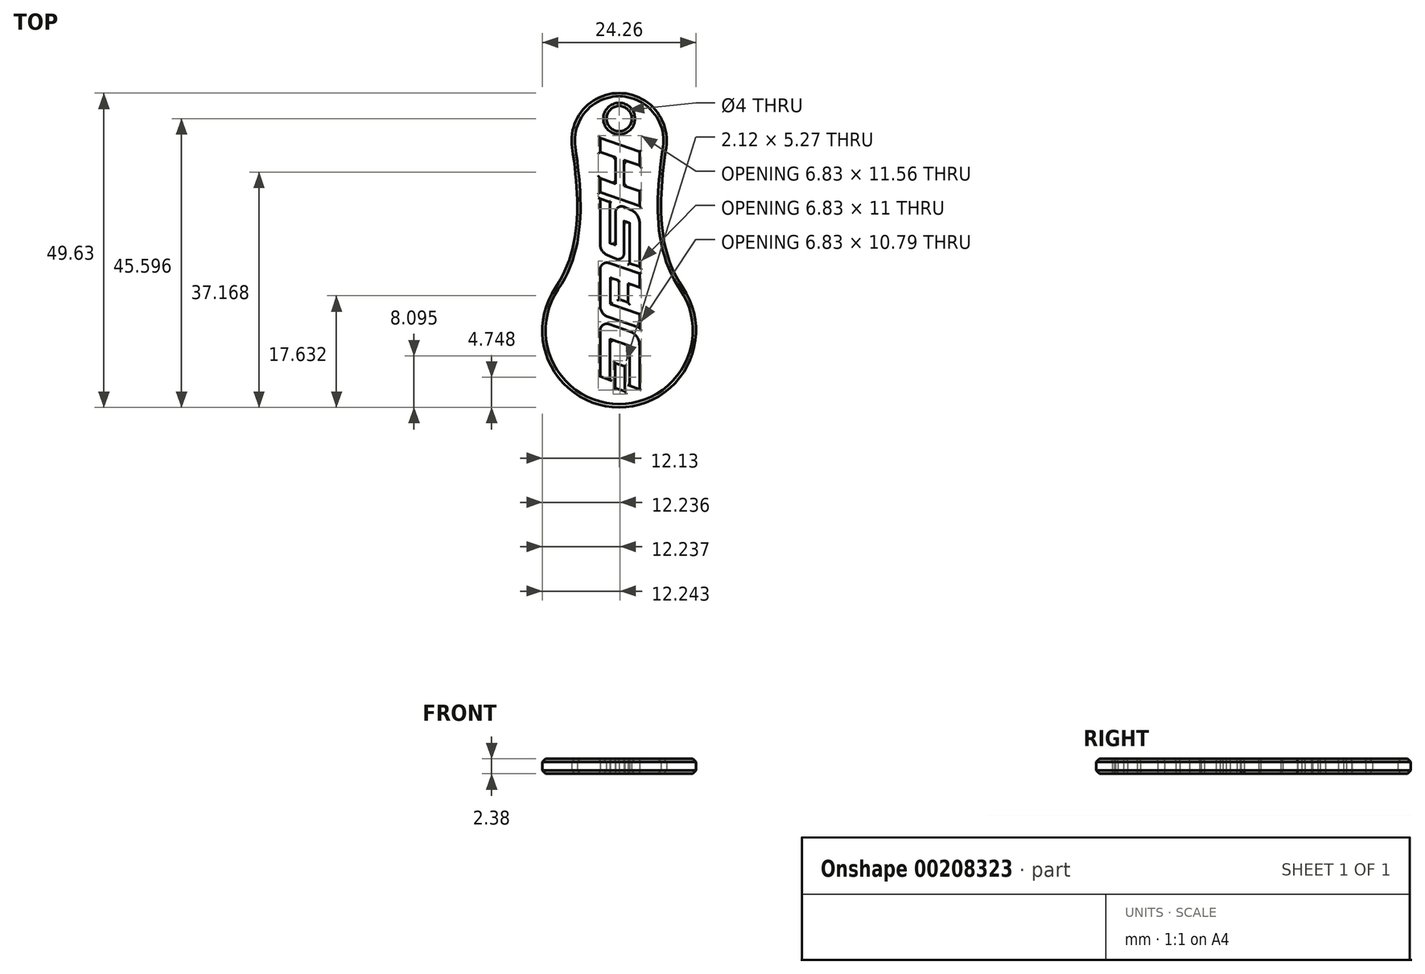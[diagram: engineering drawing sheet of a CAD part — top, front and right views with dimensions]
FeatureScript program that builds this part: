
annotation { "Feature Type Name" : "Feature", "Feature Type Description" : "" }
export const myFeature = defineFeature(function(context is Context, id is Id, definition is map)
    precondition{}
    {
        {
            var Q0;
            Q0=qCreatedBy(makeId("Top.planeOp"),FACE);
            var sketch = newSketch(context, id + "F0", { "sketchPlane" : qUnion([Q0])});
            skArc(sketch, "E0", {"start": v(-10.03, 6.81) * mm, "mid": v(0, -12.13) * mm, "end": v(10.03, 6.81) * mm});
            skLineSegment(sketch, "E1", {"start": v(0, 0) * mm, "end": v(0, 30) * mm, "construction": true});
            skArc(sketch, "E2", {"start": v(7.42, 28.91) * mm, "mid": v(0, 37.5) * mm, "end": v(-7.42, 28.91) * mm});
            skFitSpline(sketch, "E3", {"points": [v(-7.42, 28.91) * mm, v(-10.03, 6.81) * mm], "startDerivative": vector(3.56, -24.3) * mm, "endDerivative": vector(-12.7, -18.7) * mm});
            skFitSpline(sketch, "E4.MirrorCS", {"points": [v(7.42, 28.91) * mm, v(10.03, 6.81) * mm], "startDerivative": vector(-3.56, -24.3) * mm, "endDerivative": vector(12.7, -18.7) * mm});
            skLineSegment(sketch, "E5", {"start": v(-3.01, -7.2) * mm, "end": v(-3.01, -0.01) * mm});
            skLineSegment(sketch, "E6", {"start": v(-1.58, 1) * mm, "end": v(1.63, -0.1) * mm});
            skLineSegment(sketch, "E7", {"start": v(3.22, -2.34) * mm, "end": v(3.22, -9.31) * mm});
            skLineSegment(sketch, "E8", {"start": v(3.22, -9.31) * mm, "end": v(1.64, -8.7) * mm});
            skLineSegment(sketch, "E9", {"start": v(1.64, -8.7) * mm, "end": v(1.64, -2.43) * mm});
            skLineSegment(sketch, "E10", {"start": v(1.64, -2.43) * mm, "end": v(-1.44, -1.36) * mm});
            skLineSegment(sketch, "E11", {"start": v(-1.44, -1.36) * mm, "end": v(-1.44, -7.82) * mm});
            skLineSegment(sketch, "E12", {"start": v(-1.44, -7.82) * mm, "end": v(-3.01, -7.2) * mm});
            skLineSegment(sketch, "E13", {"start": v(-0.65, -9.1) * mm, "end": v(-0.65, -5.16) * mm});
            skLineSegment(sketch, "E14", {"start": v(-0.65, -5.16) * mm, "end": v(0.87, -5.66) * mm});
            skLineSegment(sketch, "E15", {"start": v(0.87, -5.66) * mm, "end": v(0.87, -9.6) * mm});
            skLineSegment(sketch, "E16", {"start": v(0.87, -9.6) * mm, "end": v(-0.65, -9.1) * mm});
            skLineSegment(sketch, "E17", {"start": v(3.22, 0.42) * mm, "end": v(-1.73, 2.14) * mm});
            skLineSegment(sketch, "E18", {"start": v(-3.01, 3.94) * mm, "end": v(-3.01, 9.62) * mm});
            skLineSegment(sketch, "E19", {"start": v(-1.57, 10.65) * mm, "end": v(3.22, 8.99) * mm});
            skLineSegment(sketch, "E20", {"start": v(3.22, 8.99) * mm, "end": v(3.22, 6.8) * mm});
            skLineSegment(sketch, "E21", {"start": v(3.22, 6.8) * mm, "end": v(1.39, 7.43) * mm});
            skLineSegment(sketch, "E22", {"start": v(1.39, 7.43) * mm, "end": v(1.39, 4.45) * mm});
            skLineSegment(sketch, "E23", {"start": v(1.39, 4.45) * mm, "end": v(0, 4.93) * mm});
            skLineSegment(sketch, "E24", {"start": v(0, 4.93) * mm, "end": v(0, 7.86) * mm});
            skLineSegment(sketch, "E25", {"start": v(0, 7.86) * mm, "end": v(-1.42, 8.35) * mm});
            skLineSegment(sketch, "E26", {"start": v(-1.42, 8.35) * mm, "end": v(-1.42, 4.2) * mm});
            skLineSegment(sketch, "E27", {"start": v(-1.42, 4.2) * mm, "end": v(3.21, 2.58) * mm});
            skLineSegment(sketch, "E28", {"start": v(3.21, 2.58) * mm, "end": v(3.22, 0.42) * mm});
            skLineSegment(sketch, "E29", {"start": v(-3.01, 20.83) * mm, "end": v(-3.01, 13.65) * mm});
            skLineSegment(sketch, "E30", {"start": v(-1.9, 11.94) * mm, "end": v(-0.54, 11.33) * mm});
            skLineSegment(sketch, "E31", {"start": v(0.76, 12.18) * mm, "end": v(0.76, 17.29) * mm});
            skLineSegment(sketch, "E32", {"start": v(0.76, 17.29) * mm, "end": v(1.67, 16.97) * mm});
            skLineSegment(sketch, "E33", {"start": v(1.67, 16.97) * mm, "end": v(1.67, 10.6) * mm});
            skLineSegment(sketch, "E34", {"start": v(1.67, 10.6) * mm, "end": v(3.22, 10.06) * mm});
            skLineSegment(sketch, "E35", {"start": v(3.22, 10.06) * mm, "end": v(3.22, 16.97) * mm});
            skLineSegment(sketch, "E36", {"start": v(1.86, 19.05) * mm, "end": v(0.74, 19.53) * mm});
            skLineSegment(sketch, "E37", {"start": v(-0.59, 18.65) * mm, "end": v(-0.59, 13.52) * mm});
            skLineSegment(sketch, "E38", {"start": v(-0.59, 13.52) * mm, "end": v(-1.48, 13.83) * mm});
            skLineSegment(sketch, "E39", {"start": v(-1.48, 13.83) * mm, "end": v(-1.48, 20.3) * mm});
            skLineSegment(sketch, "E40", {"start": v(-1.48, 20.3) * mm, "end": v(-3.01, 20.83) * mm});
            skLineSegment(sketch, "E41", {"start": v(-3.01, 21.82) * mm, "end": v(3.22, 19.68) * mm});
            skLineSegment(sketch, "E42", {"start": v(3.22, 19.68) * mm, "end": v(3.22, 22.03) * mm});
            skLineSegment(sketch, "E43", {"start": v(3.22, 22.03) * mm, "end": v(0.76, 22.87) * mm});
            skLineSegment(sketch, "E44", {"start": v(0.76, 22.87) * mm, "end": v(0.76, 26.92) * mm});
            skLineSegment(sketch, "E45", {"start": v(0.76, 26.92) * mm, "end": v(3.22, 26.08) * mm});
            skLineSegment(sketch, "E46", {"start": v(3.22, 26.08) * mm, "end": v(3.22, 28.25) * mm});
            skLineSegment(sketch, "E47", {"start": v(3.22, 28.25) * mm, "end": v(-3.01, 30.4) * mm});
            skLineSegment(sketch, "E48", {"start": v(-3.01, 28.16) * mm, "end": v(-0.59, 27.33) * mm});
            skLineSegment(sketch, "E49", {"start": v(-0.59, 27.33) * mm, "end": v(-0.59, 23.2) * mm});
            skLineSegment(sketch, "E50", {"start": v(-0.59, 23.2) * mm, "end": v(-3.01, 24.03) * mm});
            skLineSegment(sketch, "E51", {"start": v(-3.01, 24.03) * mm, "end": v(-3.01, 21.82) * mm});
            skPoint(sketch, "E52.visualSharp", {"position": v(-3.01, 1.5) * mm});
            skArc(sketch, "E52.filletArc", {"start": v(-1.58, 1) * mm, "mid": v(-2.56, 0.87) * mm, "end": v(-3.01, -0.01) * mm});
            skPoint(sketch, "E53.visualSharp", {"position": v(3.22, -0.66) * mm});
            skArc(sketch, "E53.filletArc", {"start": v(3.22, -2.34) * mm, "mid": v(2.78, -0.97) * mm, "end": v(1.63, -0.1) * mm});
            skPoint(sketch, "E54.visualSharp", {"position": v(-3.01, 2.58) * mm});
            skArc(sketch, "E54.filletArc", {"start": v(-3.01, 3.94) * mm, "mid": v(-2.66, 2.84) * mm, "end": v(-1.73, 2.14) * mm});
            skPoint(sketch, "E55.visualSharp", {"position": v(-3.01, 11.15) * mm});
            skArc(sketch, "E55.filletArc", {"start": v(-1.57, 10.65) * mm, "mid": v(-2.55, 10.5) * mm, "end": v(-3.01, 9.62) * mm});
            skPoint(sketch, "E56.visualSharp", {"position": v(0.76, 10.75) * mm});
            skArc(sketch, "E56.filletArc", {"start": v(-0.54, 11.33) * mm, "mid": v(0.34, 11.4) * mm, "end": v(0.76, 12.18) * mm});
            skPoint(sketch, "E57.visualSharp", {"position": v(-3.01, 12.44) * mm});
            skArc(sketch, "E57.filletArc", {"start": v(-3.01, 13.65) * mm, "mid": v(-2.7, 12.63) * mm, "end": v(-1.9, 11.94) * mm});
            skPoint(sketch, "E58.visualSharp", {"position": v(-0.59, 20.1) * mm});
            skArc(sketch, "E58.filletArc", {"start": v(0.74, 19.53) * mm, "mid": v(-0.16, 19.45) * mm, "end": v(-0.59, 18.65) * mm});
            skPoint(sketch, "E59.visualSharp", {"position": v(3.22, 18.46) * mm});
            skArc(sketch, "E59.filletArc", {"start": v(3.22, 16.97) * mm, "mid": v(2.85, 18.21) * mm, "end": v(1.86, 19.05) * mm});
            skCircle(sketch, "E60", {"center": v(0, 33.47) * mm, "radius": 2 * mm});
            skPoint(sketch, "E60.centerSnap0", {"position": v(0, 37.5) * mm});
            skLineSegment(sketch, "E61", {"start": v(-3.01, 28.16) * mm, "end": v(-3.01, 30.4) * mm});
            skSolve(sketch);
        }
        {
            var Q0;
            Q0=makeQuery(id+"F0.imprint","IMPRINT",FACE,{"disambiguationData":[TD([[makeQuery(id+"F0.imprint","IMPRINT",EDGE,{"derivedFrom":sQuery(id+"F0.wireOp",EDGE,"E0")}),1.0]])]});
            extrude(context, id + "F1", {"entities" : qUnion([Q0]), "depth" : 2.38 * mm});
        }
        {
            var Q0;
            Q0=makeQuery(id+"F1.opExtrude","CAP_EDGE",EDGE,{"disambiguationData":[OSD([sQuery(id+"F0.wireOp",EDGE,"E60")])],"isStart":false});
            var Q1;
            Q1=makeQuery(id+"F1.opExtrude","CAP_EDGE",EDGE,{"disambiguationData":[OSD([sQuery(id+"F0.wireOp",EDGE,"E60")])],"isStart":true});
            var Q2;
            Q2=makeQuery(id+"F1.opExtrude","CAP_EDGE",EDGE,{"disambiguationData":[OSD([sQuery(id+"F0.wireOp",EDGE,"E4.MirrorCS")])],"isStart":true});
            var Q3;
            Q3=makeQuery(id+"F1.opExtrude","CAP_EDGE",EDGE,{"disambiguationData":[OSD([sQuery(id+"F0.wireOp",EDGE,"E3")])],"isStart":false});
            chamfer(context, id + "F2", {"entities" : qUnion([Q0, Q1, Q2, Q3]), "width" : .5 * mm, "tangentPropagation" : true});
        }
        {
            var Q0;
            Q0=makeQuery(id+"F1.opExtrude","CAP_EDGE",EDGE,{"disambiguationData":[OSD([sQuery(id+"F0.wireOp",EDGE,"E5")])],"isStart":false});
            var Q1;
            Q1=makeQuery(id+"F1.opExtrude","CAP_EDGE",EDGE,{"disambiguationData":[OSD([sQuery(id+"F0.wireOp",EDGE,"E18")])],"isStart":false});
            var Q2;
            Q2=makeQuery(id+"F1.opExtrude","CAP_EDGE",EDGE,{"disambiguationData":[OSD([sQuery(id+"F0.wireOp",EDGE,"E29")])],"isStart":false});
            var Q3;
            Q3=makeQuery(id+"F1.opExtrude","CAP_EDGE",EDGE,{"disambiguationData":[OSD([sQuery(id+"F0.wireOp",EDGE,"E51")])],"isStart":false});
            var Q4;
            Q4=makeQuery(id+"F1.opExtrude","CAP_EDGE",EDGE,{"disambiguationData":[OSD([sQuery(id+"F0.wireOp",EDGE,"E6")])],"isStart":false});
            var Q5;
            Q5=makeQuery(id+"F1.opExtrude","CAP_EDGE",EDGE,{"disambiguationData":[OSD([sQuery(id+"F0.wireOp",EDGE,"E42")])],"isStart":false});
            var Q6;
            Q6=makeQuery(id+"F1.opExtrude","CAP_EDGE",EDGE,{"disambiguationData":[OSD([sQuery(id+"F0.wireOp",EDGE,"E46")])],"isStart":false});
            var Q7;
            Q7=makeQuery(id+"F1.opExtrude","CAP_EDGE",EDGE,{"disambiguationData":[OSD([sQuery(id+"F0.wireOp",EDGE,"E47")])],"isStart":false});
            var Q8;
            Q8=makeQuery(id+"F1.opExtrude","CAP_EDGE",EDGE,{"disambiguationData":[OSD([sQuery(id+"F0.wireOp",EDGE,"E61")])],"isStart":false});
            var Q9;
            Q9=makeQuery(id+"F1.opExtrude","CAP_EDGE",EDGE,{"disambiguationData":[OSD([sQuery(id+"F0.wireOp",EDGE,"E49")])],"isStart":false});
            var Q10;
            Q10=makeQuery(id+"F1.opExtrude","CAP_EDGE",EDGE,{"disambiguationData":[OSD([sQuery(id+"F0.wireOp",EDGE,"E48")])],"isStart":false});
            var Q11;
            Q11=makeQuery(id+"F1.opExtrude","CAP_EDGE",EDGE,{"disambiguationData":[OSD([sQuery(id+"F0.wireOp",EDGE,"E50")])],"isStart":false});
            var Q12;
            Q12=makeQuery(id+"F1.opExtrude","CAP_EDGE",EDGE,{"disambiguationData":[OSD([sQuery(id+"F0.wireOp",EDGE,"E41")])],"isStart":false});
            var Q13;
            Q13=makeQuery(id+"F1.opExtrude","CAP_EDGE",EDGE,{"disambiguationData":[OSD([sQuery(id+"F0.wireOp",EDGE,"E39")])],"isStart":false});
            var Q14;
            Q14=makeQuery(id+"F1.opExtrude","CAP_EDGE",EDGE,{"disambiguationData":[OSD([sQuery(id+"F0.wireOp",EDGE,"E58.filletArc")])],"isStart":false});
            var Q15;
            Q15=makeQuery(id+"F1.opExtrude","CAP_EDGE",EDGE,{"disambiguationData":[OSD([sQuery(id+"F0.wireOp",EDGE,"E33")])],"isStart":false});
            var Q16;
            Q16=makeQuery(id+"F1.opExtrude","CAP_EDGE",EDGE,{"disambiguationData":[OSD([sQuery(id+"F0.wireOp",EDGE,"E34")])],"isStart":false});
            var Q17;
            Q17=makeQuery(id+"F1.opExtrude","CAP_EDGE",EDGE,{"disambiguationData":[OSD([sQuery(id+"F0.wireOp",EDGE,"E24")])],"isStart":false});
            var Q18;
            Q18=makeQuery(id+"F1.opExtrude","CAP_EDGE",EDGE,{"disambiguationData":[OSD([sQuery(id+"F0.wireOp",EDGE,"E26")])],"isStart":false});
            var Q19;
            Q19=makeQuery(id+"F1.opExtrude","CAP_EDGE",EDGE,{"disambiguationData":[OSD([sQuery(id+"F0.wireOp",EDGE,"E27")])],"isStart":false});
            var Q20;
            Q20=makeQuery(id+"F1.opExtrude","CAP_EDGE",EDGE,{"disambiguationData":[OSD([sQuery(id+"F0.wireOp",EDGE,"E22")])],"isStart":false});
            var Q21;
            Q21=makeQuery(id+"F1.opExtrude","CAP_EDGE",EDGE,{"disambiguationData":[OSD([sQuery(id+"F0.wireOp",EDGE,"E20")])],"isStart":false});
            var Q22;
            Q22=makeQuery(id+"F1.opExtrude","CAP_EDGE",EDGE,{"disambiguationData":[OSD([sQuery(id+"F0.wireOp",EDGE,"E28")])],"isStart":false});
            var Q23;
            Q23=makeQuery(id+"F1.opExtrude","CAP_EDGE",EDGE,{"disambiguationData":[OSD([sQuery(id+"F0.wireOp",EDGE,"E11")])],"isStart":false});
            var Q24;
            Q24=makeQuery(id+"F1.opExtrude","CAP_EDGE",EDGE,{"disambiguationData":[OSD([sQuery(id+"F0.wireOp",EDGE,"E10")])],"isStart":false});
            var Q25;
            Q25=makeQuery(id+"F1.opExtrude","CAP_EDGE",EDGE,{"disambiguationData":[OSD([sQuery(id+"F0.wireOp",EDGE,"E9")])],"isStart":false});
            var Q26;
            Q26=makeQuery(id+"F1.opExtrude","CAP_EDGE",EDGE,{"disambiguationData":[OSD([sQuery(id+"F0.wireOp",EDGE,"E14")])],"isStart":false});
            var Q27;
            Q27=makeQuery(id+"F1.opExtrude","CAP_EDGE",EDGE,{"disambiguationData":[OSD([sQuery(id+"F0.wireOp",EDGE,"E13")])],"isStart":false});
            var Q28;
            Q28=makeQuery(id+"F1.opExtrude","CAP_EDGE",EDGE,{"disambiguationData":[OSD([sQuery(id+"F0.wireOp",EDGE,"E15")])],"isStart":false});
            var Q29;
            Q29=makeQuery(id+"F1.opExtrude","CAP_EDGE",EDGE,{"disambiguationData":[OSD([sQuery(id+"F0.wireOp",EDGE,"E16")])],"isStart":false});
            var Q30;
            Q30=makeQuery(id+"F1.opExtrude","CAP_EDGE",EDGE,{"disambiguationData":[OSD([sQuery(id+"F0.wireOp",EDGE,"E44")])],"isStart":false});
            var Q31;
            Q31=makeQuery(id+"F1.opExtrude","CAP_EDGE",EDGE,{"disambiguationData":[OSD([sQuery(id+"F0.wireOp",EDGE,"E43")])],"isStart":false});
            var Q32;
            Q32=makeQuery(id+"F1.opExtrude","CAP_EDGE",EDGE,{"disambiguationData":[OSD([sQuery(id+"F0.wireOp",EDGE,"E45")])],"isStart":false});
            var Q33;
            Q33=makeQuery(id+"F1.opExtrude","CAP_EDGE",EDGE,{"disambiguationData":[OSD([sQuery(id+"F0.wireOp",EDGE,"E23")])],"isStart":false});
            var Q34;
            Q34=makeQuery(id+"F1.opExtrude","CAP_EDGE",EDGE,{"disambiguationData":[OSD([sQuery(id+"F0.wireOp",EDGE,"E5")])],"isStart":true});
            var Q35;
            Q35=makeQuery(id+"F1.opExtrude","CAP_EDGE",EDGE,{"disambiguationData":[OSD([sQuery(id+"F0.wireOp",EDGE,"E11")])],"isStart":true});
            var Q36;
            Q36=makeQuery(id+"F1.opExtrude","CAP_EDGE",EDGE,{"disambiguationData":[OSD([sQuery(id+"F0.wireOp",EDGE,"E10")])],"isStart":true});
            var Q37;
            Q37=makeQuery(id+"F1.opExtrude","CAP_EDGE",EDGE,{"disambiguationData":[OSD([sQuery(id+"F0.wireOp",EDGE,"E9")])],"isStart":true});
            var Q38;
            Q38=makeQuery(id+"F1.opExtrude","CAP_EDGE",EDGE,{"disambiguationData":[OSD([sQuery(id+"F0.wireOp",EDGE,"E14")])],"isStart":true});
            var Q39;
            Q39=makeQuery(id+"F1.opExtrude","CAP_EDGE",EDGE,{"disambiguationData":[OSD([sQuery(id+"F0.wireOp",EDGE,"E15")])],"isStart":true});
            var Q40;
            Q40=makeQuery(id+"F1.opExtrude","CAP_EDGE",EDGE,{"disambiguationData":[OSD([sQuery(id+"F0.wireOp",EDGE,"E16")])],"isStart":true});
            var Q41;
            Q41=makeQuery(id+"F1.opExtrude","CAP_EDGE",EDGE,{"disambiguationData":[OSD([sQuery(id+"F0.wireOp",EDGE,"E13")])],"isStart":true});
            var Q42;
            Q42=makeQuery(id+"F1.opExtrude","CAP_EDGE",EDGE,{"disambiguationData":[OSD([sQuery(id+"F0.wireOp",EDGE,"E18")])],"isStart":true});
            var Q43;
            Q43=makeQuery(id+"F1.opExtrude","CAP_EDGE",EDGE,{"disambiguationData":[OSD([sQuery(id+"F0.wireOp",EDGE,"E25")])],"isStart":true});
            var Q44;
            Q44=makeQuery(id+"F1.opExtrude","CAP_EDGE",EDGE,{"disambiguationData":[OSD([sQuery(id+"F0.wireOp",EDGE,"E21")])],"isStart":true});
            var Q45;
            Q45=makeQuery(id+"F1.opExtrude","CAP_EDGE",EDGE,{"disambiguationData":[OSD([sQuery(id+"F0.wireOp",EDGE,"E20")])],"isStart":true});
            var Q46;
            Q46=makeQuery(id+"F1.opExtrude","CAP_EDGE",EDGE,{"disambiguationData":[OSD([sQuery(id+"F0.wireOp",EDGE,"E22")])],"isStart":true});
            var Q47;
            Q47=makeQuery(id+"F1.opExtrude","CAP_EDGE",EDGE,{"disambiguationData":[OSD([sQuery(id+"F0.wireOp",EDGE,"E24")])],"isStart":true});
            var Q48;
            Q48=makeQuery(id+"F1.opExtrude","CAP_EDGE",EDGE,{"disambiguationData":[OSD([sQuery(id+"F0.wireOp",EDGE,"E27")])],"isStart":true});
            var Q49;
            Q49=makeQuery(id+"F1.opExtrude","CAP_EDGE",EDGE,{"disambiguationData":[OSD([sQuery(id+"F0.wireOp",EDGE,"E26")])],"isStart":true});
            var Q50;
            Q50=makeQuery(id+"F1.opExtrude","CAP_EDGE",EDGE,{"disambiguationData":[OSD([sQuery(id+"F0.wireOp",EDGE,"E28")])],"isStart":true});
            var Q51;
            Q51=makeQuery(id+"F1.opExtrude","CAP_EDGE",EDGE,{"disambiguationData":[OSD([sQuery(id+"F0.wireOp",EDGE,"E23")])],"isStart":true});
            var Q52;
            Q52=makeQuery(id+"F1.opExtrude","CAP_EDGE",EDGE,{"disambiguationData":[OSD([sQuery(id+"F0.wireOp",EDGE,"E57.filletArc")])],"isStart":true});
            var Q53;
            Q53=makeQuery(id+"F1.opExtrude","CAP_EDGE",EDGE,{"disambiguationData":[OSD([sQuery(id+"F0.wireOp",EDGE,"E35")])],"isStart":true});
            var Q54;
            Q54=makeQuery(id+"F1.opExtrude","CAP_EDGE",EDGE,{"disambiguationData":[OSD([sQuery(id+"F0.wireOp",EDGE,"E32")])],"isStart":true});
            var Q55;
            Q55=makeQuery(id+"F1.opExtrude","CAP_EDGE",EDGE,{"disambiguationData":[OSD([sQuery(id+"F0.wireOp",EDGE,"E38")])],"isStart":true});
            var Q56;
            Q56=makeQuery(id+"F1.opExtrude","CAP_EDGE",EDGE,{"disambiguationData":[OSD([sQuery(id+"F0.wireOp",EDGE,"E40")])],"isStart":true});
            var Q57;
            Q57=makeQuery(id+"F1.opExtrude","CAP_EDGE",EDGE,{"disambiguationData":[OSD([sQuery(id+"F0.wireOp",EDGE,"E50")])],"isStart":true});
            var Q58;
            Q58=makeQuery(id+"F1.opExtrude","CAP_EDGE",EDGE,{"disambiguationData":[OSD([sQuery(id+"F0.wireOp",EDGE,"E51")])],"isStart":true});
            var Q59;
            Q59=makeQuery(id+"F1.opExtrude","CAP_EDGE",EDGE,{"disambiguationData":[OSD([sQuery(id+"F0.wireOp",EDGE,"E41")])],"isStart":true});
            var Q60;
            Q60=makeQuery(id+"F1.opExtrude","CAP_EDGE",EDGE,{"disambiguationData":[OSD([sQuery(id+"F0.wireOp",EDGE,"E43")])],"isStart":true});
            var Q61;
            Q61=makeQuery(id+"F1.opExtrude","CAP_EDGE",EDGE,{"disambiguationData":[OSD([sQuery(id+"F0.wireOp",EDGE,"E42")])],"isStart":true});
            var Q62;
            Q62=makeQuery(id+"F1.opExtrude","CAP_EDGE",EDGE,{"disambiguationData":[OSD([sQuery(id+"F0.wireOp",EDGE,"E49")])],"isStart":true});
            var Q63;
            Q63=makeQuery(id+"F1.opExtrude","CAP_EDGE",EDGE,{"disambiguationData":[OSD([sQuery(id+"F0.wireOp",EDGE,"E44")])],"isStart":true});
            var Q64;
            Q64=makeQuery(id+"F1.opExtrude","CAP_EDGE",EDGE,{"disambiguationData":[OSD([sQuery(id+"F0.wireOp",EDGE,"E47")])],"isStart":true});
            var Q65;
            Q65=makeQuery(id+"F1.opExtrude","CAP_EDGE",EDGE,{"disambiguationData":[OSD([sQuery(id+"F0.wireOp",EDGE,"E61")])],"isStart":true});
            var Q66;
            Q66=makeQuery(id+"F1.opExtrude","CAP_EDGE",EDGE,{"disambiguationData":[OSD([sQuery(id+"F0.wireOp",EDGE,"E48")])],"isStart":true});
            var Q67;
            Q67=makeQuery(id+"F1.opExtrude","CAP_EDGE",EDGE,{"disambiguationData":[OSD([sQuery(id+"F0.wireOp",EDGE,"E45")])],"isStart":true});
            var Q68;
            Q68=makeQuery(id+"F1.opExtrude","CAP_EDGE",EDGE,{"disambiguationData":[OSD([sQuery(id+"F0.wireOp",EDGE,"E46")])],"isStart":true});
            fillet(context, id + "F3", {"entities" : qUnion([Q0, Q1, Q2, Q3, Q4, Q5, Q6, Q7, Q8, Q9, Q10, Q11, Q12, Q13, Q14, Q15, Q16, Q17, Q18, Q19, Q20, Q21, Q22, Q23, Q24, Q25, Q26, Q27, Q28, Q29, Q30, Q31, Q32, Q33, Q34, Q35, Q36, Q37, Q38, Q39, Q40, Q41, Q42, Q43, Q44, Q45, Q46, Q47, Q48, Q49, Q50, Q51, Q52, Q53, Q54, Q55, Q56, Q57, Q58, Q59, Q60, Q61, Q62, Q63, Q64, Q65, Q66, Q67, Q68]), "radius" : .3 * mm, "tangentPropagation" : true, "allowEdgeOverflow" : false});
        }
    });
